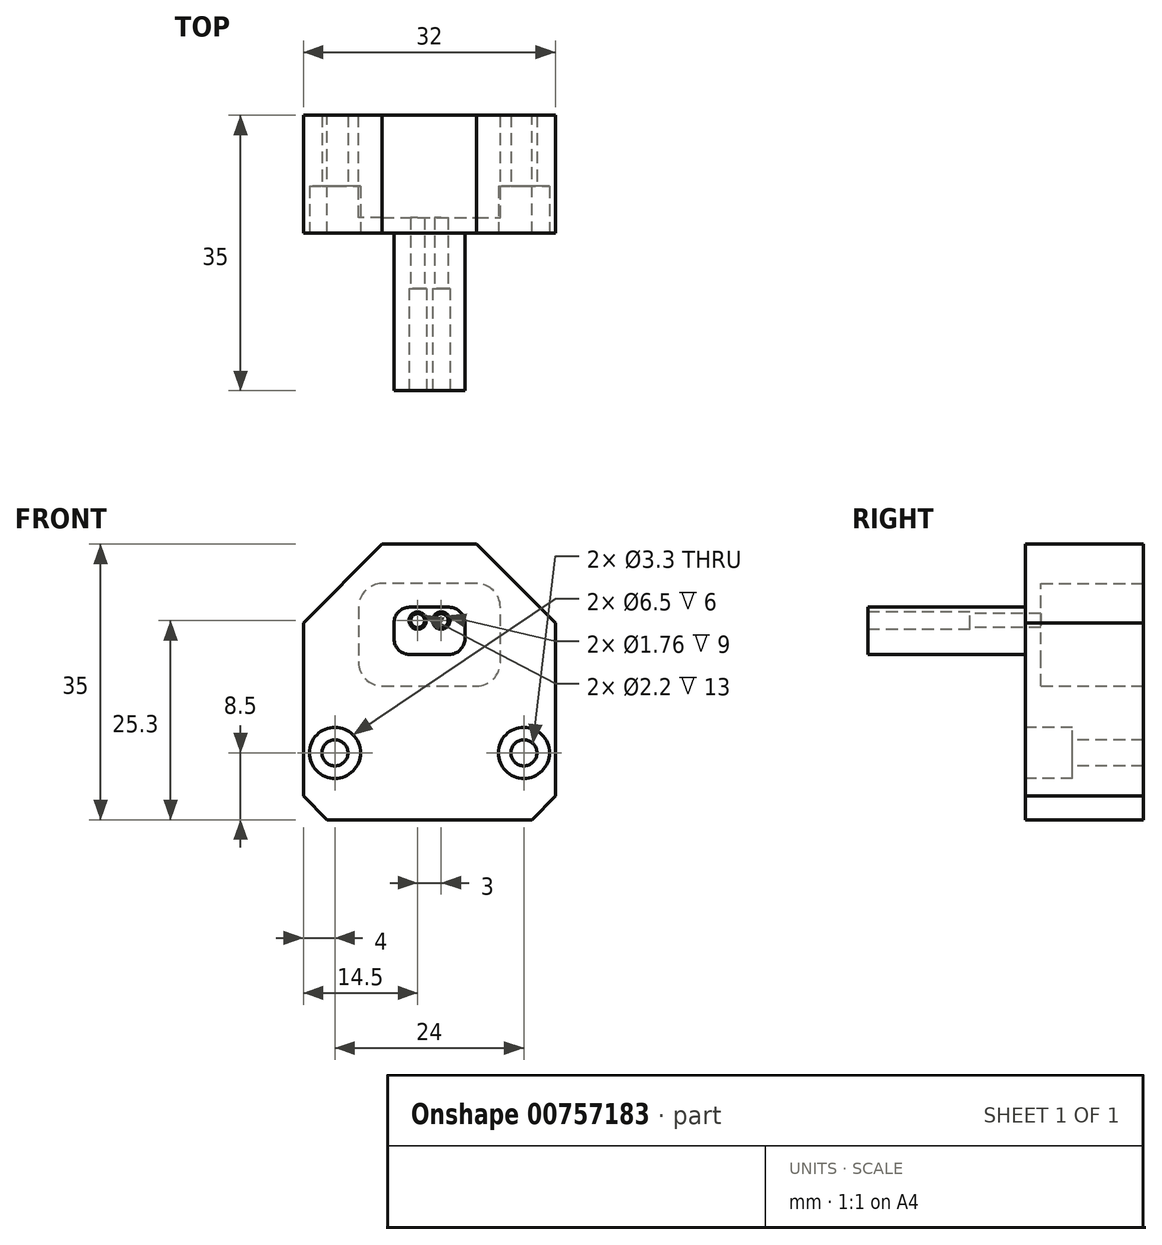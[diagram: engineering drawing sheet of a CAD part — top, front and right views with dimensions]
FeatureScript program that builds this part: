
annotation { "Feature Type Name" : "Feature", "Feature Type Description" : "" }
export const myFeature = defineFeature(function(context is Context, id is Id, definition is map)
    precondition{}
    {
        {
            var Q0;
            Q0=qCreatedBy(makeId("Front.planeOp"),FACE);
            var sketch = newSketch(context, id + "F0", { "sketchPlane" : qUnion([Q0])});
            skLineSegment(sketch, "E0.bottom", {"start": v(10, 0) * mm, "end": v(22, 0) * mm});
            skLineSegment(sketch, "E0.top", {"start": v(3, -35) * mm, "end": v(29, -35) * mm});
            skLineSegment(sketch, "E0.left", {"start": v(0, -10) * mm, "end": v(0, -32) * mm});
            skLineSegment(sketch, "E0.right", {"start": v(32, -10) * mm, "end": v(32, -32) * mm});
            skPoint(sketch, "E1", {"position": v(0, -10) * mm});
            skPoint(sketch, "E2", {"position": v(10, 0) * mm});
            skPoint(sketch, "E3", {"position": v(22, 0) * mm});
            skPoint(sketch, "E4", {"position": v(32, -10) * mm});
            skPoint(sketch, "E5", {"position": v(32, -32) * mm});
            skPoint(sketch, "E6", {"position": v(0, -32) * mm});
            skPoint(sketch, "E7", {"position": v(3, -35) * mm});
            skPoint(sketch, "E8", {"position": v(29, -35) * mm});
            skLineSegment(sketch, "E9", {"start": v(0, -10) * mm, "end": v(10, 0) * mm});
            skLineSegment(sketch, "E10", {"start": v(22, 0) * mm, "end": v(32, -10) * mm});
            skLineSegment(sketch, "E11", {"start": v(32, -32) * mm, "end": v(29, -35) * mm});
            skLineSegment(sketch, "E12", {"start": v(0, -32) * mm, "end": v(3, -35) * mm});
            skPoint(sketch, "E13.orphan", {"position": v(0, 0) * mm});
            skPoint(sketch, "E14.orphan", {"position": v(32, 0) * mm});
            skPoint(sketch, "E15.orphan", {"position": v(32, -35) * mm});
            skPoint(sketch, "E16.orphan", {"position": v(0, -35) * mm});
            skSolve(sketch);
        }
        {
            var Q0;
            Q0=makeQuery(id+"F0.imprint","IMPRINT",FACE,{"disambiguationData":[TD([[makeQuery(id+"F0.imprint","IMPRINT",EDGE,{"derivedFrom":sQuery(id+"F0.wireOp",EDGE,"E0.bottom")}),-1.0]])]});
            extrude(context, id + "F1", {"entities" : qUnion([Q0]), "depth" : 15 * mm, "offsetDistance" : 25 * mm});
        }
        {
            var Q0;
            Q0=makeQuery(id+"F1.opExtrude","CAP_FACE",FACE,{"disambiguationData":[OSD([sQuery(id+"F0.wireOp",EDGE,"E0.bottom"),sQuery(id+"F0.wireOp",EDGE,"E0.top"),sQuery(id+"F0.wireOp",EDGE,"E0.left"),sQuery(id+"F0.wireOp",EDGE,"E0.right"),sQuery(id+"F0.wireOp",EDGE,"E9"),sQuery(id+"F0.wireOp",EDGE,"E10"),sQuery(id+"F0.wireOp",EDGE,"E11"),sQuery(id+"F0.wireOp",EDGE,"E12")])],"isStart":false});
            var sketch = newSketch(context, id + "F2", { "sketchPlane" : qUnion([Q0])});
            skPoint(sketch, "E17", {"position": v(11.5, -8) * mm});
            skPoint(sketch, "E18", {"position": v(20.5, -8) * mm});
            skPoint(sketch, "E19", {"position": v(20.5, -14) * mm});
            skPoint(sketch, "E20", {"position": v(11.5, -14) * mm});
            skPoint(sketch, "E21", {"position": v(4, -26.5) * mm});
            skPoint(sketch, "E22", {"position": v(28, -26.5) * mm});
            skLineSegment(sketch, "E23", {"start": v(11.5, -8) * mm, "end": v(20.5, -8) * mm});
            skLineSegment(sketch, "E24", {"start": v(20.5, -8) * mm, "end": v(20.5, -14) * mm});
            skLineSegment(sketch, "E25", {"start": v(20.5, -14) * mm, "end": v(11.5, -14) * mm});
            skLineSegment(sketch, "E26", {"start": v(11.5, -14) * mm, "end": v(11.5, -8) * mm});
            skSolve(sketch);
        }
        {
            var Q0;
            Q0=makeQuery(id+"F2.imprint","IMPRINT",FACE,{"disambiguationData":[TD([[makeQuery(id+"F2.imprint","IMPRINT",EDGE,{"derivedFrom":sQuery(id+"F2.wireOp",EDGE,"E23")}),-1.0]])]});
            extrude(context, id + "F3", {"entities" : qUnion([Q0]), "operationType" : NewBodyOperationType.ADD, "depth" : (20) * mm, "offsetDistance" : 25 * mm});
        }
        {
            var Q0;
            Q0=makeQuery(id+"F1.opExtrude","CAP_FACE",FACE,{"disambiguationData":[OSD([sQuery(id+"F0.wireOp",EDGE,"E0.bottom"),sQuery(id+"F0.wireOp",EDGE,"E0.top"),sQuery(id+"F0.wireOp",EDGE,"E0.left"),sQuery(id+"F0.wireOp",EDGE,"E0.right"),sQuery(id+"F0.wireOp",EDGE,"E9"),sQuery(id+"F0.wireOp",EDGE,"E10"),sQuery(id+"F0.wireOp",EDGE,"E11"),sQuery(id+"F0.wireOp",EDGE,"E12")])],"isStart":true});
            var sketch = newSketch(context, id + "F4", { "sketchPlane" : qUnion([Q0])});
            skPoint(sketch, "E27", {"position": v(-25, -5) * mm});
            skPoint(sketch, "E28", {"position": v(-7, -5) * mm});
            skPoint(sketch, "E29", {"position": v(-7, -18) * mm});
            skPoint(sketch, "E30", {"position": v(-25, -18) * mm});
            skLineSegment(sketch, "E31", {"start": v(-25, -5) * mm, "end": v(-7, -5) * mm});
            skLineSegment(sketch, "E32", {"start": v(-7, -18) * mm, "end": v(-25, -18) * mm});
            skLineSegment(sketch, "E33", {"start": v(-25, -18) * mm, "end": v(-25, -5) * mm});
            skLineSegment(sketch, "E34", {"start": v(-7, -5) * mm, "end": v(-7, -18) * mm});
            skSolve(sketch);
        }
        {
            var Q0;
            Q0=makeQuery(id+"F4.imprint","IMPRINT",FACE,{"disambiguationData":[TD([[makeQuery(id+"F4.imprint","IMPRINT",EDGE,{"derivedFrom":sQuery(id+"F4.wireOp",EDGE,"E31")}),-1.0]])]});
            extrude(context, id + "F5", {"entities" : qUnion([Q0]), "operationType" : NewBodyOperationType.REMOVE, "oppositeDirection" : true, "depth" : 13 * mm, "offsetDistance" : 25 * mm});
        }
        {
            var Q0;
            Q0=makeQuery(id+"F5.boolean.opBoolean","COPY",EDGE,{"derivedFrom":makeQuery(id+"F5.opExtrude","SWEPT_EDGE",EDGE,{"disambiguationData":[OSD([sQuery(id+"F4.wireOp",EDGE,"E31"),sQuery(id+"F4.wireOp",EDGE,"E33")])]})});
            var Q1;
            Q1=makeQuery(id+"F5.boolean.opBoolean","COPY",EDGE,{"derivedFrom":makeQuery(id+"F5.opExtrude","SWEPT_EDGE",EDGE,{"disambiguationData":[OSD([sQuery(id+"F4.wireOp",EDGE,"E31"),sQuery(id+"F4.wireOp",EDGE,"E34")])]})});
            var Q2;
            Q2=makeQuery(id+"F5.boolean.opBoolean","COPY",EDGE,{"derivedFrom":makeQuery(id+"F5.opExtrude","SWEPT_EDGE",EDGE,{"disambiguationData":[OSD([sQuery(id+"F4.wireOp",EDGE,"E32"),sQuery(id+"F4.wireOp",EDGE,"E33")])]})});
            var Q3;
            Q3=makeQuery(id+"F5.boolean.opBoolean","COPY",EDGE,{"derivedFrom":makeQuery(id+"F5.opExtrude","SWEPT_EDGE",EDGE,{"disambiguationData":[OSD([sQuery(id+"F4.wireOp",EDGE,"E32"),sQuery(id+"F4.wireOp",EDGE,"E34")])]})});
            fillet(context, id + "F6", {"entities" : qUnion([Q0, Q1, Q2, Q3]), "radius" : 3 * mm, "tangentPropagation" : true, "allowEdgeOverflow" : false});
        }
        {
            var Q0;
            Q0=sQuery(id+"F2.wireOp",VERTEX,"E21");
            var Q1;
            Q1=sQuery(id+"F2.wireOp",VERTEX,"E22");
            var Q2;
            Q2=makeQuery(id+"F1.opExtrude","SWEPT_BODY",BODY,{"disambiguationData":[OSD([sQuery(id+"F0.wireOp",EDGE,"E0.bottom"),sQuery(id+"F0.wireOp",EDGE,"E0.top"),sQuery(id+"F0.wireOp",EDGE,"E0.left"),sQuery(id+"F0.wireOp",EDGE,"E0.right"),sQuery(id+"F0.wireOp",EDGE,"E9"),sQuery(id+"F0.wireOp",EDGE,"E10"),sQuery(id+"F0.wireOp",EDGE,"E11"),sQuery(id+"F0.wireOp",EDGE,"E12")])]});
            hole(context, id + "F7", {"style" : HoleStyle.C_BORE, "endStyle" : HoleEndStyle.THROUGH, "holeDiameter" : 3.3 * mm, "cBoreDiameter" : 6.5 * mm, "cBoreDepth" : 6 * mm, "majorDiameter" : 5 * mm, "isTappedThrough" : true, "tappedDepth" : 13.25 * mm, "tapClearance" : 3, "locations" : qUnion([Q0, Q1]), "scope" : qUnion([Q2])});
        }
        {
            var Q0;
            Q0=makeQuery(id+"F3.opExtrude","CAP_FACE",FACE,{"disambiguationData":[OSD([sQuery(id+"F2.wireOp",EDGE,"E23"),sQuery(id+"F2.wireOp",EDGE,"E24"),sQuery(id+"F2.wireOp",EDGE,"E25"),sQuery(id+"F2.wireOp",EDGE,"E26")])],"isStart":false});
            var sketch = newSketch(context, id + "F8", { "sketchPlane" : qUnion([Q0])});
            skPoint(sketch, "E35", {"position": v(19.06, -8) * mm});
            skPoint(sketch, "E36", {"position": v(17.5, -9.7) * mm});
            skPoint(sketch, "E37", {"position": v(14.5, -9.7) * mm});
            skSolve(sketch);
        }
        {
            var Q0;
            Q0=sQuery(id+"F8.wireOp",VERTEX,"E37");
            var Q1;
            Q1=sQuery(id+"F8.wireOp",VERTEX,"E36");
            var Q2;
            Q2=makeQuery(id+"F1.opExtrude","SWEPT_BODY",BODY,{"disambiguationData":[OSD([sQuery(id+"F0.wireOp",EDGE,"E0.bottom"),sQuery(id+"F0.wireOp",EDGE,"E0.top"),sQuery(id+"F0.wireOp",EDGE,"E0.left"),sQuery(id+"F0.wireOp",EDGE,"E0.right"),sQuery(id+"F0.wireOp",EDGE,"E9"),sQuery(id+"F0.wireOp",EDGE,"E10"),sQuery(id+"F0.wireOp",EDGE,"E11"),sQuery(id+"F0.wireOp",EDGE,"E12")])]});
            hole(context, id + "F9", {"style" : HoleStyle.C_BORE, "endStyle" : HoleEndStyle.THROUGH, "holeDiameter" : 1.76 * mm, "cBoreDiameter" : 2.2 * mm, "cBoreDepth" : 13 * mm, "majorDiameter" : 5 * mm, "isTappedThrough" : true, "tappedDepth" : 13.25 * mm, "tapClearance" : 3, "locations" : qUnion([Q0, Q1]), "scope" : qUnion([Q2])});
        }
        {
            var Q0;
            Q0=makeQuery(id+"F3.opExtrude","SWEPT_EDGE",EDGE,{"disambiguationData":[OSD([sQuery(id+"F2.wireOp",EDGE,"E23"),sQuery(id+"F2.wireOp",EDGE,"E24")])]});
            var Q1;
            Q1=makeQuery(id+"F3.opExtrude","SWEPT_EDGE",EDGE,{"disambiguationData":[OSD([sQuery(id+"F2.wireOp",EDGE,"E24"),sQuery(id+"F2.wireOp",EDGE,"E25")])]});
            var Q2;
            Q2=makeQuery(id+"F3.opExtrude","SWEPT_EDGE",EDGE,{"disambiguationData":[OSD([sQuery(id+"F2.wireOp",EDGE,"E23"),sQuery(id+"F2.wireOp",EDGE,"E26")])]});
            var Q3;
            Q3=makeQuery(id+"F3.opExtrude","SWEPT_EDGE",EDGE,{"disambiguationData":[OSD([sQuery(id+"F2.wireOp",EDGE,"E25"),sQuery(id+"F2.wireOp",EDGE,"E26")])]});
            fillet(context, id + "F10", {"entities" : qUnion([Q0, Q1, Q2, Q3]), "radius" : 2 * mm, "tangentPropagation" : true, "allowEdgeOverflow" : false});
        }
    });
